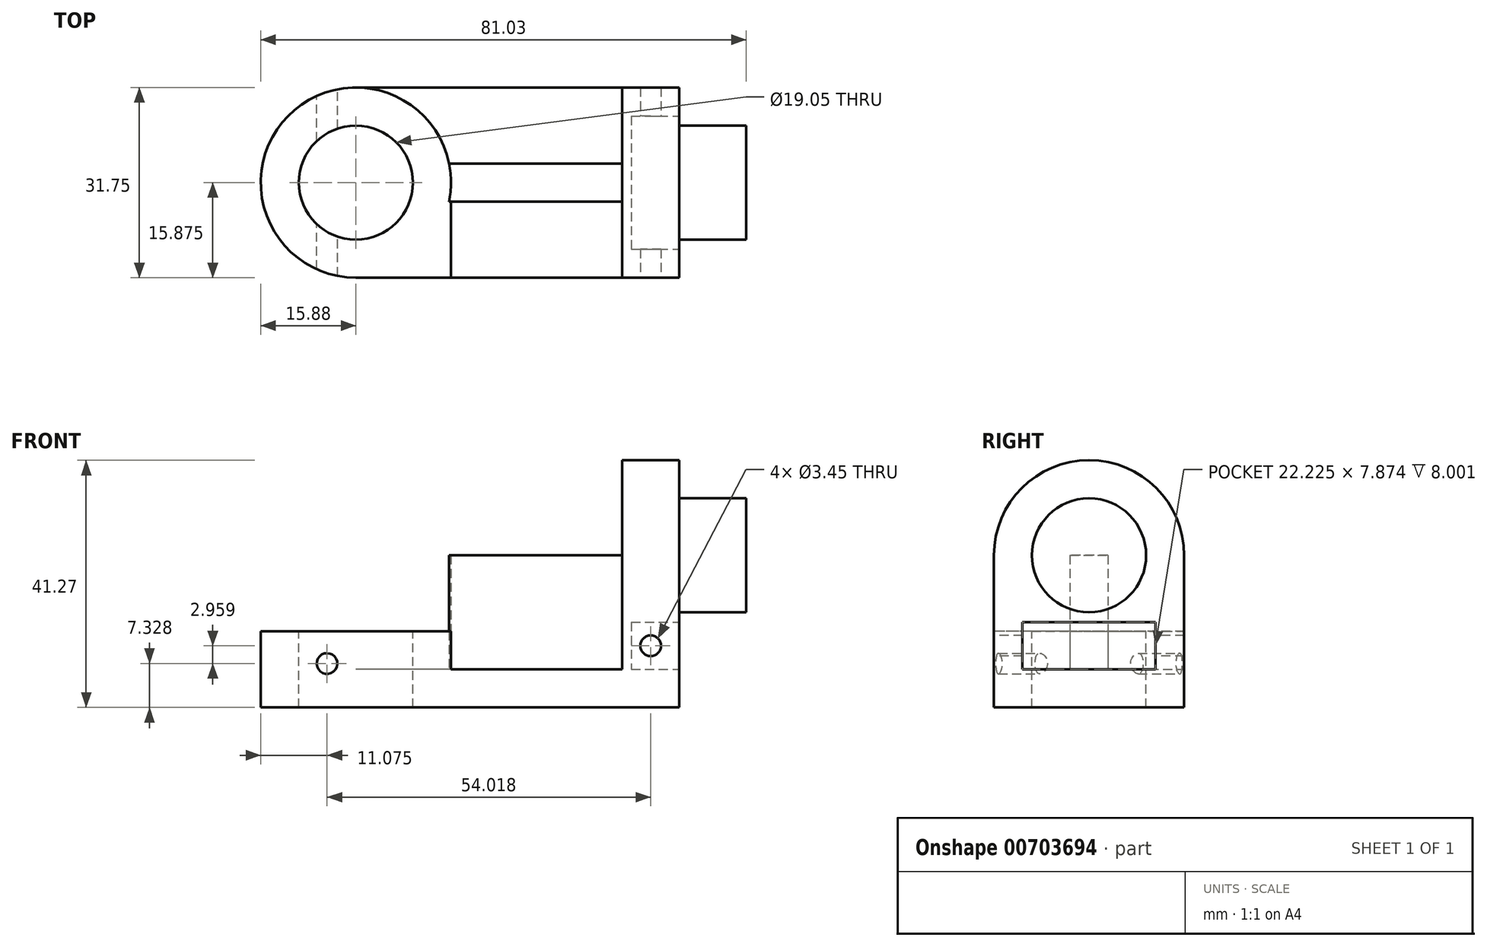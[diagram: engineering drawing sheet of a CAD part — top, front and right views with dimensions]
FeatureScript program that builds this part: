
annotation { "Feature Type Name" : "Feature", "Feature Type Description" : "" }
export const myFeature = defineFeature(function(context is Context, id is Id, definition is map)
    precondition{}
    {
        {
            var Q0;
            Q0=qCreatedBy(makeId("Top.planeOp"),FACE);
            var sketch = newSketch(context, id + "F0", { "sketchPlane" : qUnion([Q0])});
            skLineSegment(sketch, "E0", {"start": v(0, 0) * mm, "end": v(53.98, 0) * mm});
            skLineSegment(sketch, "E1", {"start": v(53.98, 0) * mm, "end": v(53.98, 31.75) * mm});
            skLineSegment(sketch, "E2", {"start": v(53.98, 31.75) * mm, "end": v(0, 31.75) * mm});
            skArc(sketch, "E3", {"start": v(0, 31.75) * mm, "mid": v(-15.88, 15.87) * mm, "end": v(0, 0) * mm});
            skSolve(sketch);
        }
        {
            var Q0;
            Q0 = qSketchRegion(id + "F0", true);
            extrude(context, id + "F1", {"entities" : qUnion([Q0]), "depth" : 41.27 * mm, "offsetDistance" : 25.4 * mm});
        }
        {
            var Q0;
            Q0=makeQuery(id+"F1.opExtrude","SWEPT_FACE",FACE,{"disambiguationData":[OSD([sQuery(id+"F0.wireOp",EDGE,"E0")])]});
            var sketch = newSketch(context, id + "F2", { "sketchPlane" : qUnion([Q0])});
            skLineSegment(sketch, "E4", {"start": v(44.45, 41.28) * mm, "end": v(44.45, 6.35) * mm});
            skLineSegment(sketch, "E5", {"start": v(44.45, 6.35) * mm, "end": v(15.88, 6.35) * mm});
            skLineSegment(sketch, "E6", {"start": v(15.88, 6.35) * mm, "end": v(15.88, 12.7) * mm});
            skLineSegment(sketch, "E7", {"start": v(15.88, 12.7) * mm, "end": v(-15.88, 12.7) * mm});
            skLineSegment(sketch, "E8", {"start": v(-15.88, 12.7) * mm, "end": v(-15.88, 41.28) * mm});
            skLineSegment(sketch, "E9", {"start": v(-15.88, 41.28) * mm, "end": v(44.45, 41.28) * mm});
            skSolve(sketch);
        }
        {
            var Q0;
            Q0 = qSketchRegion(id + "F2", true);
            extrude(context, id + "F3", {"entities" : qUnion([Q0]), "operationType" : NewBodyOperationType.REMOVE, "endBound" : BoundingType.THROUGH_ALL, "oppositeDirection" : true, "depth" : 25.4 * mm, "offsetDistance" : 25.4 * mm});
        }
        {
            var Q0;
            Q0=makeQuery(id+"F1.opExtrude","SWEPT_FACE",FACE,{"disambiguationData":[OSD([sQuery(id+"F0.wireOp",EDGE,"E1")])]});
            var sketch = newSketch(context, id + "F4", { "sketchPlane" : qUnion([Q0])});
            skArc(sketch, "E10", {"start": v(31.75, 25.4) * mm, "mid": v(15.88, 41.28) * mm, "end": v(0, 25.4) * mm});
            skLineSegment(sketch, "E11", {"start": v(0, 25.4) * mm, "end": v(0, 0) * mm});
            skLineSegment(sketch, "E12", {"start": v(0, 0) * mm, "end": v(31.75, 0) * mm});
            skLineSegment(sketch, "E13", {"start": v(31.75, 0) * mm, "end": v(31.75, 25.4) * mm});
            skSolve(sketch);
        }
        {
            var Q0;
            {var subQ0=sQuery(id+"F4.wireOp",EDGE,"E10");var subQ1=sQuery(id+"F0.wireOp",EDGE,"E1");var subQ4=makeQuery(id+"F1.opExtrude","CAP_EDGE",EDGE,{"disambiguationData":[OSD([subQ1])],"isStart":false});var subQ5=makeQuery(id+"F4.imprint","INTERSECT",VERTEX,{"derivedFrom":[subQ4,subQ0]});Q0=makeQuery(id+"F4.imprint","IMPRINT",FACE,{"disambiguationData":[TD([[makeQuery(id+"F4.imprint","IMPRINT",EDGE,{"disambiguationData":[TD([[subQ5,1.0]])],"derivedFrom":subQ4}),-1.0]])]});}
            var Q1;
            {var subQ0=sQuery(id+"F4.wireOp",EDGE,"E10");var subQ1=sQuery(id+"F0.wireOp",EDGE,"E1");var subQ4=makeQuery(id+"F1.opExtrude","CAP_EDGE",EDGE,{"disambiguationData":[OSD([subQ1])],"isStart":false});var subQ5=makeQuery(id+"F4.imprint","INTERSECT",VERTEX,{"derivedFrom":[subQ4,subQ0]});Q1=makeQuery(id+"F4.imprint","IMPRINT",FACE,{"disambiguationData":[TD([[makeQuery(id+"F4.imprint","IMPRINT",EDGE,{"disambiguationData":[TD([[subQ5,-1.0]])],"derivedFrom":subQ4}),-1.0]])]});}
            extrude(context, id + "F5", {"entities" : qUnion([Q0, Q1]), "operationType" : NewBodyOperationType.REMOVE, "endBound" : BoundingType.THROUGH_ALL, "oppositeDirection" : true, "depth" : 25.4 * mm, "offsetDistance" : 25.4 * mm});
        }
        {
            var Q0;
            Q0=makeQuery(id+"F1.opExtrude","SWEPT_FACE",FACE,{"disambiguationData":[OSD([sQuery(id+"F0.wireOp",EDGE,"E1")])]});
            var sketch = newSketch(context, id + "F6", { "sketchPlane" : qUnion([Q0])});
            skLineSegment(sketch, "E14", {"start": v(4.76, 14.22) * mm, "end": v(4.76, 6.35) * mm});
            skLineSegment(sketch, "E15", {"start": v(4.76, 6.35) * mm, "end": v(26.99, 6.35) * mm});
            skLineSegment(sketch, "E16", {"start": v(26.99, 6.35) * mm, "end": v(26.99, 14.22) * mm});
            skLineSegment(sketch, "E17", {"start": v(26.99, 14.22) * mm, "end": v(4.76, 14.22) * mm});
            skLineSegment(sketch, "E18", {"start": v(15.88, 41.28) * mm, "end": v(15.88, 0) * mm, "construction": true});
            skSolve(sketch);
        }
        {
            var Q0;
            Q0 = qSketchRegion(id + "F6", true);
            extrude(context, id + "F7", {"entities" : qUnion([Q0]), "operationType" : NewBodyOperationType.REMOVE, "oppositeDirection" : true, "depth" : 8 * mm, "offsetDistance" : 25.4 * mm});
        }
        {
            var Q0;
            Q0=makeQuery(id+"F1.opExtrude","SWEPT_FACE",FACE,{"disambiguationData":[OSD([sQuery(id+"F0.wireOp",EDGE,"E1")])]});
            var sketch = newSketch(context, id + "F8", { "sketchPlane" : qUnion([Q0])});
            skCircle(sketch, "E19", {"center": v(15.88, 25.4) * mm, "radius": 9.53 * mm});
            skSolve(sketch);
        }
        {
            var Q0;
            Q0 = qSketchRegion(id + "F8", true);
            extrude(context, id + "F9", {"entities" : qUnion([Q0]), "operationType" : NewBodyOperationType.ADD, "depth" : 11.18 * mm, "offsetDistance" : 25.4 * mm});
        }
        {
            var Q0;
            Q0=makeQuery(id+"F1.opExtrude","SWEPT_FACE",FACE,{"disambiguationData":[OSD([sQuery(id+"F0.wireOp",EDGE,"E0")])]});
            var sketch = newSketch(context, id + "F10", { "sketchPlane" : qUnion([Q0])});
            skCircle(sketch, "E20", {"center": v(49.21, 10.29) * mm, "radius": 1.73 * mm});
            skSolve(sketch);
        }
        {
            var Q0;
            Q0 = qSketchRegion(id + "F10", true);
            extrude(context, id + "F11", {"entities" : qUnion([Q0]), "operationType" : NewBodyOperationType.REMOVE, "endBound" : BoundingType.THROUGH_ALL, "oppositeDirection" : true, "depth" : 25.4 * mm, "offsetDistance" : 25.4 * mm});
        }
        {
            var Q0;
            Q0=makeQuery(id+"F3.boolean.opBoolean","COPY",FACE,{"derivedFrom":makeQuery(id+"F3.opExtrude","SWEPT_FACE",FACE,{"disambiguationData":[OSD([sQuery(id+"F2.wireOp",EDGE,"E7")])]})});
            var sketch = newSketch(context, id + "F12", { "sketchPlane" : qUnion([Q0])});
            skCircle(sketch, "E21", {"center": v(0, 15.88) * mm, "radius": 15.88 * mm});
            skSolve(sketch);
        }
        {
            var Q0;
            {var subQ1=sQuery(id+"F2.wireOp",EDGE,"E7");var subQ2=makeQuery(id+"F3.boolean.opBoolean","INTERSECT",EDGE,{"derivedFrom":[makeQuery(id+"F1.opExtrude","SWEPT_FACE",FACE,{"disambiguationData":[OSD([sQuery(id+"F0.wireOp",EDGE,"E2")])]}),makeQuery(id+"F3.opExtrude","SWEPT_FACE",FACE,{"disambiguationData":[OSD([subQ1])]})]});Q0=makeQuery(id+"F12.imprint","IMPRINT",FACE,{"disambiguationData":[TD([[makeQuery(id+"F12.imprint","IMPRINT",EDGE,{"derivedFrom":subQ2}),1.0]])]});}
            var Q1;
            {var subQ1=sQuery(id+"F2.wireOp",EDGE,"E7");var subQ2=makeQuery(id+"F3.boolean.opBoolean","COPY",EDGE,{"derivedFrom":makeQuery(id+"F3.opExtrude","CAP_EDGE",EDGE,{"disambiguationData":[OSD([subQ1])],"isStart":true})});Q1=makeQuery(id+"F12.imprint","IMPRINT",FACE,{"disambiguationData":[TD([[makeQuery(id+"F12.imprint","IMPRINT",EDGE,{"derivedFrom":subQ2}),-1.0]])]});}
            extrude(context, id + "F13", {"entities" : qUnion([Q0, Q1]), "operationType" : NewBodyOperationType.REMOVE, "oppositeDirection" : true, "depth" : 6.35 * mm, "offsetDistance" : 25.4 * mm});
        }
        {
            var Q0;
            Q0=makeQuery(id+"F3.boolean.opBoolean","COPY",FACE,{"derivedFrom":makeQuery(id+"F3.opExtrude","SWEPT_FACE",FACE,{"disambiguationData":[OSD([sQuery(id+"F2.wireOp",EDGE,"E7")])]})});
            var sketch = newSketch(context, id + "F14", { "sketchPlane" : qUnion([Q0])});
            skCircle(sketch, "E22", {"center": v(0, 15.88) * mm, "radius": 9.53 * mm});
            skSolve(sketch);
        }
        {
            var Q0;
            Q0 = qSketchRegion(id + "F14", true);
            extrude(context, id + "F15", {"entities" : qUnion([Q0]), "operationType" : NewBodyOperationType.REMOVE, "endBound" : BoundingType.THROUGH_ALL, "oppositeDirection" : true, "depth" : 25.4 * mm, "offsetDistance" : 25.4 * mm});
        }
        {
            var Q0;
            Q0=qCreatedBy(makeId("Top.planeOp"),FACE);
            var sketch = newSketch(context, id + "F16", { "sketchPlane" : qUnion([Q0])});
            skLineSegment(sketch, "E23", {"start": v(15.55, 19.05) * mm, "end": v(44.45, 19.05) * mm});
            skLineSegment(sketch, "E24", {"start": v(44.45, 19.05) * mm, "end": v(44.45, 12.7) * mm});
            skLineSegment(sketch, "E25", {"start": v(44.45, 12.7) * mm, "end": v(15.55, 12.7) * mm});
            skArc(sketch, "E26", {"start": v(15.55, 12.7) * mm, "mid": v(15.88, 15.88) * mm, "end": v(15.55, 19.05) * mm});
            skPoint(sketch, "E27.endSnap0", {"position": v(15.88, 15.88) * mm});
            skLineSegment(sketch, "E28", {"start": v(0, 15.88) * mm, "end": v(44.45, 15.88) * mm, "construction": true});
            skSolve(sketch);
        }
        {
            var Q0;
            Q0 = qSketchRegion(id + "F16", true);
            extrude(context, id + "F17", {"entities" : qUnion([Q0]), "operationType" : NewBodyOperationType.ADD, "depth" : 25.4 * mm, "offsetDistance" : 25.4 * mm});
        }
        {
            var Q0;
            Q0=makeQuery(id+"F1.opExtrude","SWEPT_FACE",FACE,{"disambiguationData":[OSD([sQuery(id+"F0.wireOp",EDGE,"E2")])]});
            var sketch = newSketch(context, id + "F18", { "sketchPlane" : qUnion([Q0])});
            skCircle(sketch, "E29", {"center": v(4.8, 7.33) * mm, "radius": 1.73 * mm});
            skSolve(sketch);
        }
        {
            var Q0;
            Q0 = qSketchRegion(id + "F18", true);
            extrude(context, id + "F19", {"entities" : qUnion([Q0]), "operationType" : NewBodyOperationType.REMOVE, "endBound" : BoundingType.THROUGH_ALL, "oppositeDirection" : true, "depth" : 25.4 * mm, "offsetDistance" : 25.4 * mm});
        }
    });
